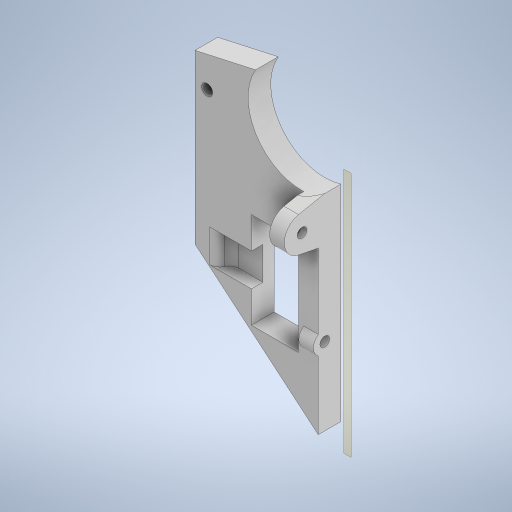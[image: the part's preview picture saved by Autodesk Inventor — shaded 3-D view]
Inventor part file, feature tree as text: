
AUTODESK INVENTOR PART (.ipt)
format: ipt  version: 2023 (Build 270158000, 158)  size: 399,360 bytes
history: native  units: in
note: dims shown in document units (in); Inventor stores cm internally (conversion verified against a paired STEP export)
features: reference x18, sketch x17, other x10, extrude x5, hole x3, projected_geometry x2, fillet x1
ambient origin geometry x8: Origin, YZ Plane, XZ Plane, XY Plane, X Axis, Y Axis, Z Axis, Center Point
bodies: Body1 (feature_tree)
feature tree (56):
  other  "SCIANA_2.0.ipt"
  extrude  "Wyciągnięcie proste1"  Depth=0.3937in
  extrude  "Wyciągnięcie proste2"  Depth=0.2362in
  extrude  "Wyciągnięcie proste3"  Depth=0.3937in TaperAngle=0.0deg
  fillet  "Zaokrąglenie1"  Radius=0.1378in
  hole  "Otwór1"  [1 undecoded]
  extrude  "Wyciągnięcie proste4"  Depth=0.1378in TaperAngle=0.0deg
  sketch  "Szkic16"
  hole  "Otwór2"  [1 undecoded]
  extrude  "Wyciągnięcie proste5"  Depth=0.1181in
  hole  "Otwór3"  [1 undecoded]
  other  "Bryła1::SCIANA_2.0.ipt"
  other  "Bryła wyprowadzona1"
  sketch  "Szkic1"
  sketch  "Szkic2"
  sketch  "Szkic3"
  sketch  "Szkic4"
  sketch  "Szkic5"
  sketch  "Szkic6"
  sketch  "Szkic7"
  sketch  "Szkic8"
  sketch  "Szkic9"
  sketch  "Szkic10"
  other  "Płaszczyzna konstrukcyjna1"
  other  "Płaszczyzna konstrukcyjna2"
  sketch  "Szkic11"
  reference  "Odniesienie1"
  reference  "Odniesienie2"
  reference  "Odniesienie3"
  reference  "Odniesienie4"
  reference  "Odniesienie5"
  reference  "Odniesienie6"
  reference  "Odniesienie7"
  reference  "Odniesienie8"
  reference  "Odniesienie9"
  sketch  "Szkic12"
  reference  "Odniesienie10"
  sketch  "Szkic13"
  reference  "Odniesienie11"
  reference  "Odniesienie12"
  sketch  "Szkic14"
  reference  "Odniesienie13"
  reference  "Odniesienie14"
  reference  "Odniesienie15"
  sketch  "Szkic15"
  reference  "Odniesienie16"
  reference  "Odniesienie17"
  reference  "Odniesienie18"
  projected_geometry  "Pętla rzutowana1"
  sketch  "Szkic17"
  projected_geometry  "Pętla rzutowana2"
  other  "Bryła1"
  other  "GP2Y0A41SK0F_MIR1:1"
  other  "SCIANA_2.0:1"
  other  "mocowanie_serw:1"
  other  "pokrywka:1"
note: 3 required parameter values undecoded (feature->parameter linkage not recoverable at this tier; creation-order binding heuristic only, values carry confidence <= 0.55)
